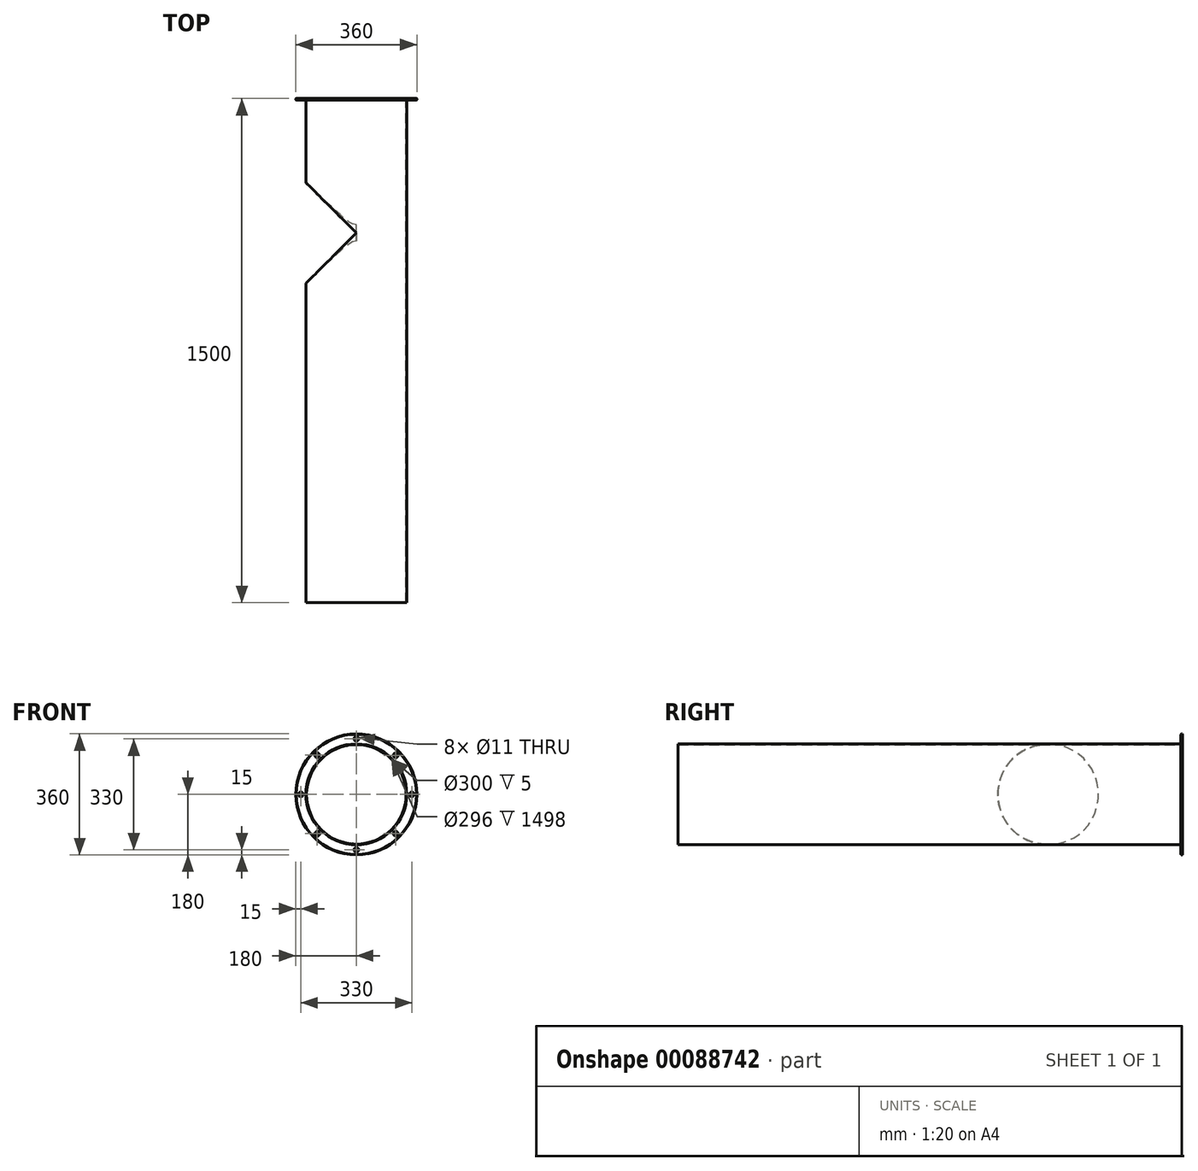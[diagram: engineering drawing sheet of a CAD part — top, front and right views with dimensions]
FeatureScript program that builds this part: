
annotation { "Feature Type Name" : "Feature", "Feature Type Description" : "" }
export const myFeature = defineFeature(function(context is Context, id is Id, definition is map)
    precondition{}
    {
        {
            var Q0;
            Q0=qCreatedBy(makeId("Front.planeOp"),FACE);
            var sketch = newSketch(context, id + "F0", { "sketchPlane" : qUnion([Q0])});
            skCircle(sketch, "E0", {"center": v(0, 0) * mm, "radius": 180 * mm});
            skCircle(sketch, "E1", {"center": v(0, 0) * mm, "radius": 150 * mm});
            skCircle(sketch, "E2", {"center": v(0, 0) * mm, "radius": 148 * mm});
            skCircle(sketch, "E3", {"center": v(-165, 0) * mm, "radius": 5.5 * mm});
            skCircle(sketch, "E4", {"center": v(-116.62, 116.73) * mm, "radius": 5.5 * mm});
            skCircle(sketch, "E5", {"center": v(0, 165) * mm, "radius": 5.5 * mm});
            skCircle(sketch, "E6", {"center": v(117.19, 116.16) * mm, "radius": 5.5 * mm});
            skCircle(sketch, "E7", {"center": v(165, 0) * mm, "radius": 5.5 * mm});
            skCircle(sketch, "E8", {"center": v(116.73, -116.62) * mm, "radius": 5.5 * mm});
            skCircle(sketch, "E9", {"center": v(0, -165) * mm, "radius": 5.5 * mm});
            skCircle(sketch, "E10", {"center": v(-116.16, -117.19) * mm, "radius": 5.5 * mm});
            skSolve(sketch);
        }
        {
            var Q0;
            Q0=makeQuery(id+"F0.imprint","IMPRINT",FACE,{"disambiguationData":[TD([[makeQuery(id+"F0.imprint","IMPRINT",EDGE,{"derivedFrom":sQuery(id+"F0.wireOp",EDGE,"E1")}),1.0]])]});
            extrude(context, id + "F1", {"entities" : qUnion([Q0]), "depth" : 1500 * mm});
        }
        {
            var Q0;
            Q0 = qSketchRegion(id + "F0", true);
            var Q1;
            Q1=makeQuery(id+"F0.imprint","IMPRINT",FACE,{"disambiguationData":[TD([[makeQuery(id+"F0.imprint","IMPRINT",EDGE,{"derivedFrom":sQuery(id+"F0.wireOp",EDGE,"E1")}),-1.0]])]});
            extrude(context, id + "F2", {"entities" : qUnion([Q0, Q1]), "depth" : 5 * mm});
        }
        {
            var Q0;
            Q0=makeQuery(id+"F1.opExtrude","CAP_EDGE",EDGE,{"disambiguationData":[OSD([sQuery(id+"F0.wireOp",EDGE,"E2")])],"isStart":true});
            fillet(context, id + "F3", {"entities" : qUnion([Q0]), "radius" : 2 * mm, "tangentPropagation" : true, "allowEdgeOverflow" : false});
        }
        {
            var Q0;
            Q0=makeQuery(id+"F2.opExtrude","CAP_EDGE",EDGE,{"disambiguationData":[OSD([sQuery(id+"F0.wireOp",EDGE,"E0")])],"isStart":false});
            var Q1;
            Q1=makeQuery(id+"F2.opExtrude","CAP_EDGE",EDGE,{"disambiguationData":[OSD([sQuery(id+"F0.wireOp",EDGE,"E0")])],"isStart":true});
            var Q2;
            Q2=makeQuery(id+"F2.opExtrude","CAP_EDGE",EDGE,{"disambiguationData":[OSD([sQuery(id+"F0.wireOp",EDGE,"E7")])],"isStart":true});
            var Q3;
            Q3=makeQuery(id+"F2.opExtrude","CAP_EDGE",EDGE,{"disambiguationData":[OSD([sQuery(id+"F0.wireOp",EDGE,"E6")])],"isStart":true});
            var Q4;
            Q4=makeQuery(id+"F2.opExtrude","CAP_EDGE",EDGE,{"disambiguationData":[OSD([sQuery(id+"F0.wireOp",EDGE,"E6")])],"isStart":false});
            var Q5;
            Q5=makeQuery(id+"F2.opExtrude","CAP_EDGE",EDGE,{"disambiguationData":[OSD([sQuery(id+"F0.wireOp",EDGE,"E7")])],"isStart":false});
            var Q6;
            Q6=makeQuery(id+"F2.opExtrude","CAP_EDGE",EDGE,{"disambiguationData":[OSD([sQuery(id+"F0.wireOp",EDGE,"E8")])],"isStart":false});
            var Q7;
            Q7=makeQuery(id+"F2.opExtrude","CAP_EDGE",EDGE,{"disambiguationData":[OSD([sQuery(id+"F0.wireOp",EDGE,"E10")])],"isStart":false});
            var Q8;
            Q8=makeQuery(id+"F2.opExtrude","CAP_EDGE",EDGE,{"disambiguationData":[OSD([sQuery(id+"F0.wireOp",EDGE,"E3")])],"isStart":false});
            var Q9;
            Q9=makeQuery(id+"F2.opExtrude","CAP_EDGE",EDGE,{"disambiguationData":[OSD([sQuery(id+"F0.wireOp",EDGE,"E4")])],"isStart":false});
            var Q10;
            Q10=makeQuery(id+"F2.opExtrude","CAP_EDGE",EDGE,{"disambiguationData":[OSD([sQuery(id+"F0.wireOp",EDGE,"E5")])],"isStart":false});
            var Q11;
            Q11=makeQuery(id+"F2.opExtrude","CAP_EDGE",EDGE,{"disambiguationData":[OSD([sQuery(id+"F0.wireOp",EDGE,"E10")])],"isStart":true});
            var Q12;
            Q12=makeQuery(id+"F2.opExtrude","CAP_EDGE",EDGE,{"disambiguationData":[OSD([sQuery(id+"F0.wireOp",EDGE,"E3")])],"isStart":true});
            var Q13;
            Q13=makeQuery(id+"F2.opExtrude","CAP_EDGE",EDGE,{"disambiguationData":[OSD([sQuery(id+"F0.wireOp",EDGE,"E4")])],"isStart":true});
            var Q14;
            Q14=makeQuery(id+"F2.opExtrude","CAP_EDGE",EDGE,{"disambiguationData":[OSD([sQuery(id+"F0.wireOp",EDGE,"E5")])],"isStart":true});
            var Q15;
            Q15=makeQuery(id+"F2.opExtrude","CAP_EDGE",EDGE,{"disambiguationData":[OSD([sQuery(id+"F0.wireOp",EDGE,"E9")])],"isStart":true});
            var Q16;
            Q16=makeQuery(id+"F2.opExtrude","CAP_EDGE",EDGE,{"disambiguationData":[OSD([sQuery(id+"F0.wireOp",EDGE,"E8")])],"isStart":true});
            var Q17;
            Q17=makeQuery(id+"F2.opExtrude","CAP_EDGE",EDGE,{"disambiguationData":[OSD([sQuery(id+"F0.wireOp",EDGE,"E5")])],"isStart":true});
            var Q18;
            Q18=makeQuery(id+"F2.opExtrude","CAP_EDGE",EDGE,{"disambiguationData":[OSD([sQuery(id+"F0.wireOp",EDGE,"E9")])],"isStart":true});
            var Q19;
            Q19=makeQuery(id+"F2.opExtrude","CAP_EDGE",EDGE,{"disambiguationData":[OSD([sQuery(id+"F0.wireOp",EDGE,"E9")])],"isStart":false});
            chamfer(context, id + "F4", {"entities" : qUnion([Q0, Q1, Q2, Q3, Q4, Q5, Q6, Q7, Q8, Q9, Q10, Q11, Q12, Q13, Q14, Q15, Q16, Q17, Q18, Q19]), "width" : 1.5 * mm, "tangentPropagation" : true});
        }
        {
            var Q0;
            Q0=qCreatedBy(makeId("Right.planeOp"),FACE);
            var sketch = newSketch(context, id + "F5", { "sketchPlane" : qUnion([Q0])});
            skLineSegment(sketch, "E11", {"start": v(0, 0) * mm, "end": v(-400, 0) * mm});
            skCircle(sketch, "E12", {"center": v(-400, 0) * mm, "radius": 150 * mm});
            skSolve(sketch);
        }
        {
            var Q0;
            Q0 = qSketchRegion(id + "F5", true);
            extrude(context, id + "F6", {"entities" : qUnion([Q0]), "operationType" : NewBodyOperationType.REMOVE, "endBound" : BoundingType.THROUGH_ALL, "oppositeDirection" : true, "depth" : 25 * mm});
        }
    });
